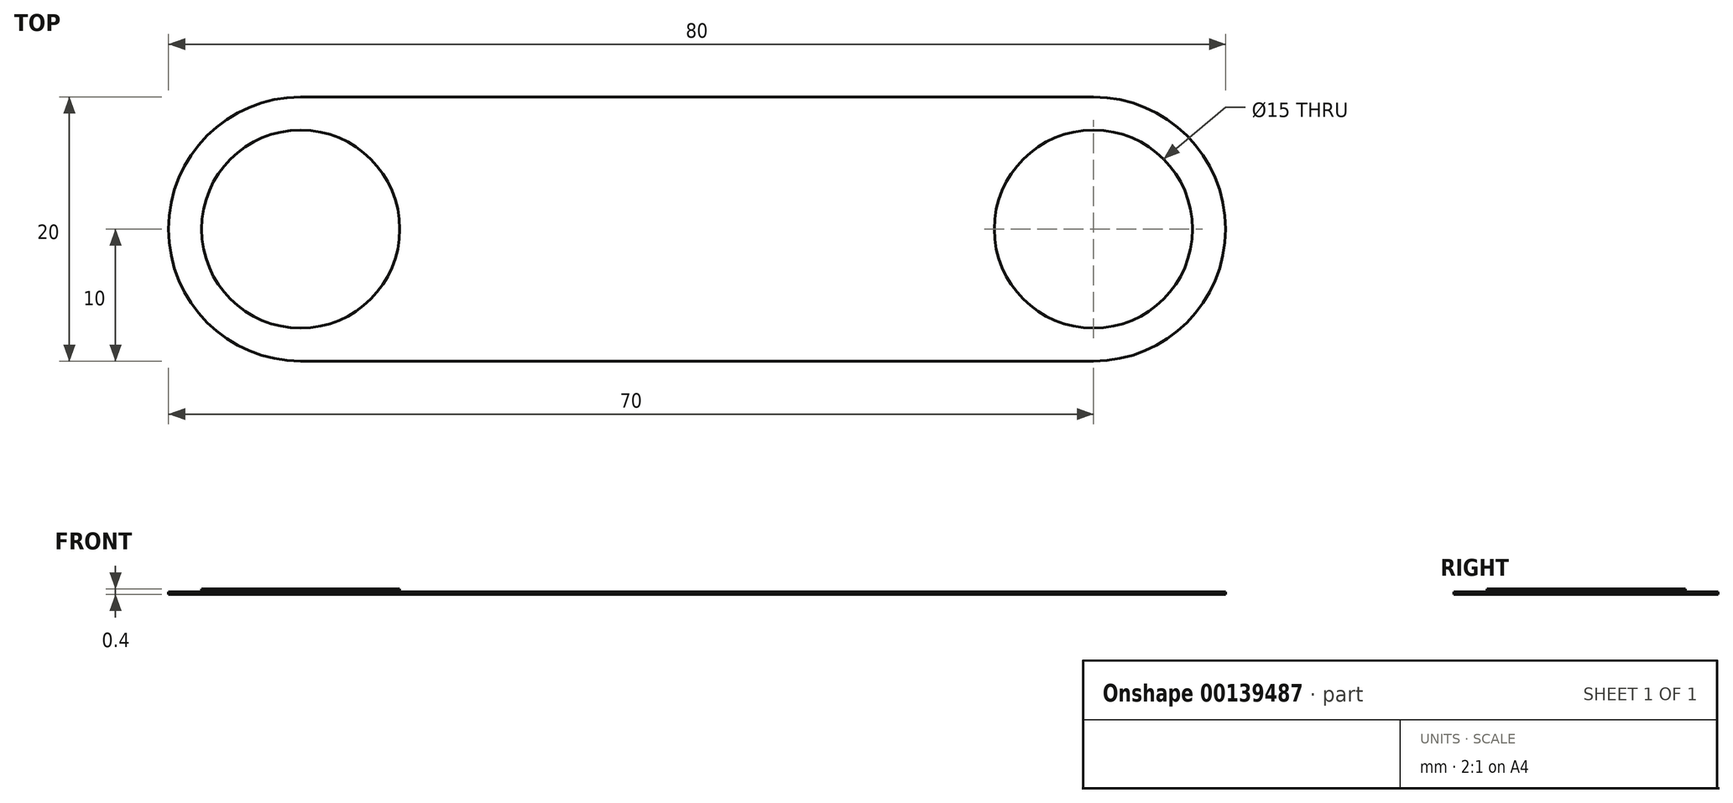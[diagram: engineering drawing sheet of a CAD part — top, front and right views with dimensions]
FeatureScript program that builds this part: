
annotation { "Feature Type Name" : "Feature", "Feature Type Description" : "" }
export const myFeature = defineFeature(function(context is Context, id is Id, definition is map)
    precondition{}
    {
        {
            assignVariable(context, id + "F0", {"name" : "depth", "anyValue" : .2});
        }
        {
            var Q0;
            Q0=qCreatedBy(makeId("Top.planeOp"),FACE);
            var sketch = newSketch(context, id + "F1", { "sketchPlane" : qUnion([Q0])});
            skLineSegment(sketch, "E0.bottom", {"start": v(30, 10) * mm, "end": v(-30, 10) * mm});
            skLineSegment(sketch, "E0.top", {"start": v(30, -10) * mm, "end": v(-30, -10) * mm});
            skPoint(sketch, "E0.middle", {"position": v(0, 0) * mm});
            skArc(sketch, "E1", {"start": v(-30, 10) * mm, "mid": v(-40, 0) * mm, "end": v(-30, -10) * mm});
            skArc(sketch, "E2", {"start": v(30, -10) * mm, "mid": v(40, 0) * mm, "end": v(30, 10) * mm});
            skSolve(sketch);
        }
        {
            var Q0;
            Q0=makeQuery(id+"F1.imprint","IMPRINT",FACE,{"disambiguationData":[TD([[makeQuery(id+"F1.imprint","IMPRINT",EDGE,{"derivedFrom":sQuery(id+"F1.wireOp",EDGE,"E0.bottom")}),1.0]])]});
            extrude(context, id + "F2", {"entities" : qUnion([Q0]), "depth" : (getVariable(context, 'depth')) * mm});
        }
        {
            var Q0;
            Q0=makeQuery(id+"F2.opExtrude","CAP_FACE",FACE,{"disambiguationData":[OSD([sQuery(id+"F1.wireOp",EDGE,"E0.bottom"),sQuery(id+"F1.wireOp",EDGE,"E0.top"),sQuery(id+"F1.wireOp",EDGE,"E1"),sQuery(id+"F1.wireOp",EDGE,"E2")])],"isStart":false});
            var sketch = newSketch(context, id + "F3", { "sketchPlane" : qUnion([Q0])});
            skCircle(sketch, "E3", {"center": v(-30, 0) * mm, "radius": 7.5 * mm});
            skCircle(sketch, "E4", {"center": v(30, 0) * mm, "radius": 7.5 * mm});
            skSolve(sketch);
        }
        {
            var Q0;
            Q0=makeQuery(id+"F3.imprint","IMPRINT",FACE,{"disambiguationData":[TD([[makeQuery(id+"F3.imprint","IMPRINT",EDGE,{"derivedFrom":sQuery(id+"F3.wireOp",EDGE,"E3")}),1.0]])]});
            extrude(context, id + "F4", {"entities" : qUnion([Q0]), "operationType" : NewBodyOperationType.ADD, "depth" : (getVariable(context, 'depth')) * mm});
        }
        {
            var Q0;
            Q0=makeQuery(id+"F3.imprint","IMPRINT",FACE,{"disambiguationData":[TD([[makeQuery(id+"F3.imprint","IMPRINT",EDGE,{"derivedFrom":sQuery(id+"F3.wireOp",EDGE,"E4")}),1.0]])]});
            extrude(context, id + "F5", {"entities" : qUnion([Q0]), "operationType" : NewBodyOperationType.ADD, "oppositeDirection" : true, "depth" : (getVariable(context, 'depth')) * mm});
        }
        {
            var Q0;
            Q0=makeQuery(id+"F3.imprint","IMPRINT",FACE,{"disambiguationData":[TD([[makeQuery(id+"F3.imprint","IMPRINT",EDGE,{"derivedFrom":sQuery(id+"F3.wireOp",EDGE,"E4")}),1.0]])]});
            extrude(context, id + "F6", {"entities" : qUnion([Q0]), "operationType" : NewBodyOperationType.REMOVE, "oppositeDirection" : true, "depth" : (getVariable(context, 'depth')) * mm});
        }
    });
